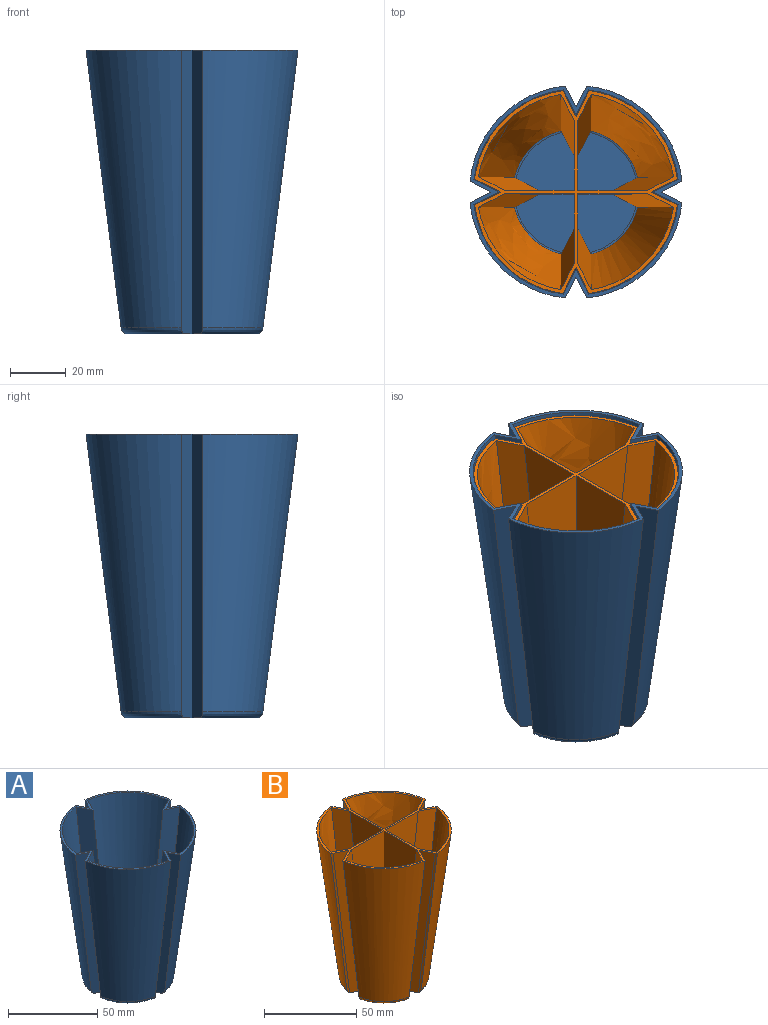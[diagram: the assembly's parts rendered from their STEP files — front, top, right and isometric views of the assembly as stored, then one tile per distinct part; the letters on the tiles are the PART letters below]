
ASSEMBLY  parts=2 mates=1
PART A: 35 faces, bbox 78.4x78.4x104.1 mm
  f0: plane 75.94x75.94mm, normal (0,0,1), area 351.4mm2, adj f2,f3,f4,f5,f6,f7,f8,f9
  f1: plane 46.03x46.03mm, normal (0,0,-1), area 1625.9mm2, adj f2,f3,f5,f6,f8,f9,f11,f12
  f2: bspline ~101.6x20.13mm, area 842.7mm2, adj f0,f1,f3,f13,f31
  f3: bspline ~101.6x20.13mm, area 842.7mm2, adj f0,f1,f2,f4,f34
  f4: bspline ~99.37x34.1mm, area 4251mm2, adj f0,f3,f5,f34
  f5: bspline ~101.6x20.13mm, area 842.7mm2, adj f0,f1,f4,f6,f34
  f6: bspline ~101.6x20.13mm, area 842.7mm2, adj f0,f1,f5,f7,f33
  f7: bspline ~99.37x34.1mm, area 4251mm2, adj f0,f6,f8,f33
  f8: bspline ~101.6x20.13mm, area 842.7mm2, adj f0,f1,f7,f9,f33
  f9: bspline ~101.6x20.13mm, area 842.7mm2, adj f0,f1,f8,f10,f32
  f10: bspline ~99.37x34.1mm, area 4251mm2, adj f0,f9,f11,f32
  f11: bspline ~101.6x20.13mm, area 842.7mm2, adj f0,f1,f10,f12,f32
  f12: bspline ~101.6x20.13mm, area 842.7mm2, adj f0,f1,f11,f13,f31
  f13: bspline ~99.37x34.1mm, area 4251mm2, adj f0,f2,f12,f31
  f14: plane 43.55x43.55mm, normal (0,0,1), area 1430.4mm2, adj f15,f16,f18,f19,f21,f22,f24,f25
  f15: offset ~104.14x24.89mm, area 988.3mm2, adj f0,f14,f16,f26,f30
  f16: offset ~104.14x24.89mm, area 988.3mm2, adj f0,f14,f15,f17,f29
  f17: offset ~104.14x36.64mm, area 3859.4mm2, adj f0,f16,f18,f29
  f18: offset ~104.14x24.89mm, area 988.3mm2, adj f0,f14,f17,f19,f29
  f19: offset ~104.14x24.89mm, area 988.3mm2, adj f0,f14,f18,f20,f27
  f20: offset ~104.14x36.64mm, area 3859.4mm2, adj f0,f19,f21,f27
  f21: offset ~104.14x24.89mm, area 988.3mm2, adj f0,f14,f20,f22,f27
  f22: offset ~104.14x24.89mm, area 988.3mm2, adj f0,f14,f21,f23,f28
  f23: offset ~104.14x36.64mm, area 3859.4mm2, adj f0,f22,f24,f28
  f24: offset ~104.14x24.89mm, area 988.3mm2, adj f0,f14,f23,f25,f28
  f25: offset ~104.14x24.89mm, area 988.3mm2, adj f0,f14,f24,f26,f30
  f26: offset ~104.14x36.64mm, area 3859.4mm2, adj f0,f15,f25,f30
  f27: bspline ~23.14x21.55mm, area 106.5mm2, adj f14,f19,f20,f21
  f28: bspline ~23.14x21.55mm, area 106.5mm2, adj f14,f22,f23,f24
  f29: bspline ~23.14x21.55mm, area 106.5mm2, adj f14,f16,f17,f18
  f30: bspline ~23.14x21.55mm, area 106.5mm2, adj f14,f15,f25,f26
  f31: bspline ~28.65x23.98mm, area 118.2mm2, adj f1,f2,f12,f13
  f32: bspline ~28.65x23.98mm, area 118.2mm2, adj f1,f9,f10,f11
  f33: bspline ~28.65x23.98mm, area 118.2mm2, adj f1,f6,f7,f8
  f34: bspline ~28.65x23.98mm, area 118.2mm2, adj f1,f3,f4,f5
PART B: 46 faces, bbox 73.8x73.8x100.3 mm
  f0: bspline ~99.06x31.03mm, area 3465mm2, adj f5,f25,f34,f43
  f1: plane 99.06x24.96mm, normal (1,0,0), area 1850.9mm2, adj f5,f6,f25,f33
  f2: bspline ~99.06x23.06mm, area 1022.8mm2, adj f4,f5,f6,f19,f45
  f3: bspline ~99.06x23.06mm, area 1022.8mm2, adj f5,f6,f16,f21,f44
  f4: bspline ~99.06x31.03mm, area 3465mm2, adj f2,f5,f14,f45
  f5: plane 73.78x73.78mm, normal (0,0,1), area 473mm2, adj f0,f1,f2,f3,f4,f7,f8,f9
  f6: plane 42.91x42.91mm, normal (0,0,-1), area 154.5mm2, adj f1,f2,f3,f7,f8,f9,f13,f14
  f7: bspline ~99.06x20.49mm, area 876.2mm2, adj f5,f6,f8,f10,f45
  f8: bspline ~99.06x20.49mm, area 876.2mm2, adj f5,f6,f7,f40,f42
  f9: bspline ~99.06x23.06mm, area 1022.8mm2, adj f5,f6,f18,f38,f42
  f10: bspline ~99.06x13.93mm, area 131.3mm2, adj f5,f7,f11,f45
  f11: bspline ~99.06x31.62mm, area 3748.4mm2, adj f5,f10,f12,f45
  f12: bspline ~99.06x13.93mm, area 131.3mm2, adj f5,f11,f13,f45
  f13: bspline ~99.06x20.49mm, area 876.2mm2, adj f5,f6,f12,f15,f45
  f14: bspline ~99.06x23.06mm, area 1022.8mm2, adj f4,f5,f6,f17,f45
  f15: bspline ~99.06x20.49mm, area 876.2mm2, adj f5,f6,f13,f24,f44
  f16: plane 99.06x24.96mm, normal (0,-1,0), area 1850.9mm2, adj f3,f5,f6,f20
  f17: plane 99.06x24.96mm, normal (0,1,0), area 1850.9mm2, adj f5,f6,f14,f19
  f18: plane 99.06x24.96mm, normal (1,0,0), area 1850.9mm2, adj f5,f6,f9,f32
  f19: plane 99.06x24.96mm, normal (-1,0,0), area 1850.9mm2, adj f2,f5,f6,f17
  f20: plane 99.06x24.96mm, normal (-1,0,0), area 1850.9mm2, adj f5,f6,f16,f30
  f21: bspline ~99.06x31.03mm, area 3465mm2, adj f3,f5,f30,f44
  f22: bspline ~99.06x31.62mm, area 3748.4mm2, adj f5,f23,f24,f44
  f23: bspline ~99.06x13.93mm, area 131.3mm2, adj f5,f22,f31,f44
  f24: bspline ~99.06x13.93mm, area 131.3mm2, adj f5,f15,f22,f44
  f25: bspline ~99.06x23.06mm, area 1022.8mm2, adj f0,f1,f5,f6,f43
  f26: bspline ~99.06x13.93mm, area 131.3mm2, adj f5,f27,f35,f43
  f27: bspline ~99.06x31.62mm, area 3748.4mm2, adj f5,f26,f28,f43
  f28: bspline ~99.06x13.93mm, area 131.3mm2, adj f5,f27,f29,f43
  f29: bspline ~99.06x20.49mm, area 876.2mm2, adj f5,f6,f28,f31,f43
  f30: bspline ~99.06x23.06mm, area 1022.8mm2, adj f5,f6,f20,f21,f44
  f31: bspline ~99.06x20.49mm, area 876.2mm2, adj f5,f6,f23,f29,f44
  f32: plane 99.06x24.96mm, normal (0,1,0), area 1850.9mm2, adj f5,f6,f18,f36
  f33: plane 99.06x24.96mm, normal (0,-1,0), area 1850.9mm2, adj f1,f5,f6,f34
  f34: bspline ~99.06x23.06mm, area 1022.8mm2, adj f0,f5,f6,f33,f43
  f35: bspline ~99.06x20.49mm, area 876.2mm2, adj f5,f6,f26,f37,f43
  f36: bspline ~99.06x23.06mm, area 1022.8mm2, adj f5,f6,f32,f38,f42
  f37: bspline ~99.06x20.49mm, area 876.2mm2, adj f5,f6,f35,f41,f42
  f38: bspline ~99.06x31.03mm, area 3465mm2, adj f5,f9,f36,f42
  f39: bspline ~99.06x31.62mm, area 3748.4mm2, adj f5,f40,f41,f42
  f40: bspline ~99.06x13.93mm, area 131.3mm2, adj f5,f8,f39,f42
  f41: bspline ~99.06x13.93mm, area 131.3mm2, adj f5,f37,f39,f42
  f42: bspline ~20.76x20.69mm, area 77.9mm2, adj f6,f8,f9,f36,f37,f38,f39,f40
  f43: bspline ~20.76x20.69mm, area 77.9mm2, adj f0,f6,f25,f26,f27,f28,f29,f34
  f44: bspline ~20.76x20.69mm, area 77.9mm2, adj f3,f6,f15,f21,f22,f23,f24,f30
  f45: bspline ~20.76x20.69mm, area 77.9mm2, adj f2,f4,f6,f7,f10,f11,f12,f13
PLACE A t=(54.64,34.98,3.88)mm fixed
PLACE B t=(54.64,34.98,3.88)mm
MATE slider A.f14 <-> B.f6  axis (0,0,1) through (54.64,34.98,-45.65)mm
